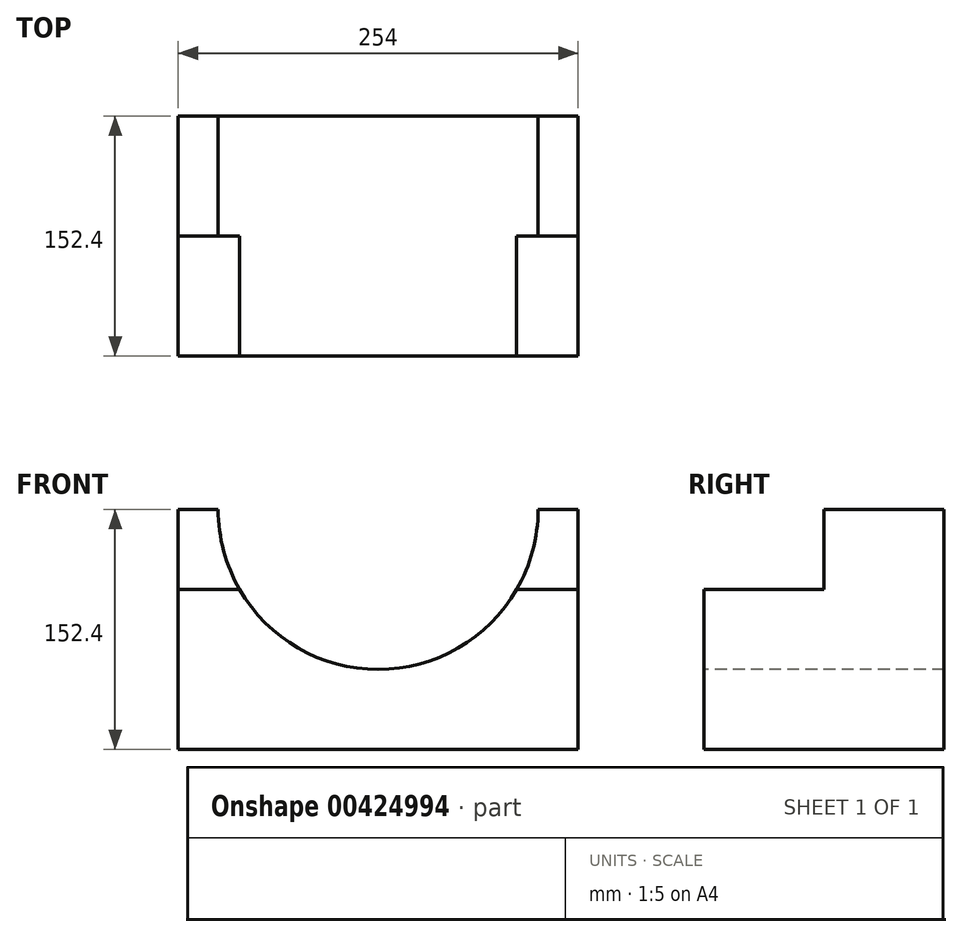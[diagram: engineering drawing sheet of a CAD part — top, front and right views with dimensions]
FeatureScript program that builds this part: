
annotation { "Feature Type Name" : "Feature", "Feature Type Description" : "" }
export const myFeature = defineFeature(function(context is Context, id is Id, definition is map)
    precondition{}
    {
        {
            var Q0;
            Q0=qCreatedBy(makeId("Top.planeOp"),FACE);
            var sketch = newSketch(context, id + "F0", { "sketchPlane" : qUnion([Q0])});
            skLineSegment(sketch, "E0.bottom", {"start": v(0, 0) * mm, "end": v(254, 0) * mm});
            skLineSegment(sketch, "E0.top", {"start": v(0, 152.4) * mm, "end": v(254, 152.4) * mm});
            skLineSegment(sketch, "E0.left", {"start": v(0, 0) * mm, "end": v(0, 152.4) * mm});
            skLineSegment(sketch, "E0.right", {"start": v(254, 0) * mm, "end": v(254, 152.4) * mm});
            skSolve(sketch);
        }
        {
            var Q0;
            Q0 = qSketchRegion(id + "F0", true);
            extrude(context, id + "F1", {"entities" : qUnion([Q0]), "depth" : 152.4 * mm});
        }
        {
            var Q0;
            Q0=makeQuery(id+"F1.opExtrude","SWEPT_FACE",FACE,{"disambiguationData":[OSD([sQuery(id+"F0.wireOp",EDGE,"E0.bottom")])]});
            var sketch = newSketch(context, id + "F2", { "sketchPlane" : qUnion([Q0])});
            skPoint(sketch, "E1", {"position": v(127, 152.4) * mm});
            skCircle(sketch, "E2", {"center": v(127, 152.4) * mm, "radius": 101.6 * mm});
            skSolve(sketch);
        }
        {
            var Q0;
            Q0 = qSketchRegion(id + "F2", true);
            extrude(context, id + "F3", {"entities" : qUnion([Q0]), "operationType" : NewBodyOperationType.REMOVE, "oppositeDirection" : true, "depth" : 152.4 * mm});
        }
        {
            var Q0;
            Q0=makeQuery(id+"F1.opExtrude","SWEPT_FACE",FACE,{"disambiguationData":[OSD([sQuery(id+"F0.wireOp",EDGE,"E0.bottom")])]});
            var sketch = newSketch(context, id + "F4", { "sketchPlane" : qUnion([Q0])});
            skLineSegment(sketch, "E3.bottom", {"start": v(0, 152.4) * mm, "end": v(254, 152.4) * mm});
            skLineSegment(sketch, "E3.top", {"start": v(0, 101.6) * mm, "end": v(254, 101.6) * mm});
            skLineSegment(sketch, "E3.left", {"start": v(0, 152.4) * mm, "end": v(0, 101.6) * mm});
            skLineSegment(sketch, "E3.right", {"start": v(254, 152.4) * mm, "end": v(254, 101.6) * mm});
            skSolve(sketch);
        }
        {
            var Q0;
            Q0 = qSketchRegion(id + "F4", true);
            extrude(context, id + "F5", {"entities" : qUnion([Q0]), "operationType" : NewBodyOperationType.REMOVE, "oppositeDirection" : true, "depth" : 76.2 * mm});
        }
    });
